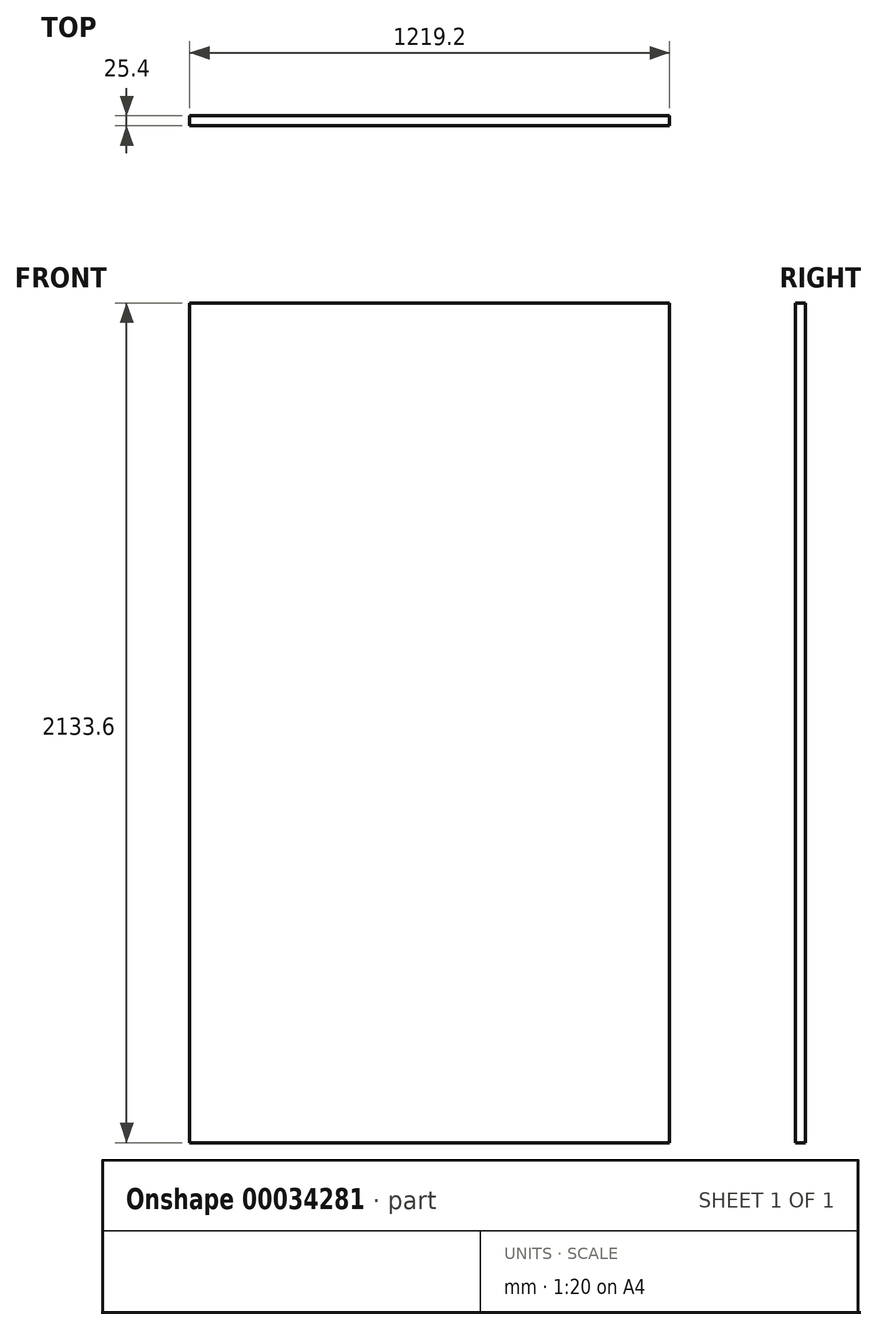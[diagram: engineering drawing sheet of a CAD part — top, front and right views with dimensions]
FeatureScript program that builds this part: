
annotation { "Feature Type Name" : "Feature", "Feature Type Description" : "" }
export const myFeature = defineFeature(function(context is Context, id is Id, definition is map)
    precondition{}
    {
        {
            var Q0;
            Q0=qCreatedBy(makeId("Front.planeOp"),FACE);
            var sketch = newSketch(context, id + "F0", { "sketchPlane" : qUnion([Q0])});
            skLineSegment(sketch, "E0.bottom", {"start": v(0, 0) * mm, "end": v(1219.2, 0) * mm});
            skLineSegment(sketch, "E0.top", {"start": v(0, 2133.6) * mm, "end": v(1219.2, 2133.6) * mm});
            skLineSegment(sketch, "E0.left", {"start": v(0, 0) * mm, "end": v(0, 2133.6) * mm});
            skLineSegment(sketch, "E0.right", {"start": v(1219.2, 0) * mm, "end": v(1219.2, 2133.6) * mm});
            skSolve(sketch);
        }
        {
            var Q0;
            Q0 = qSketchRegion(id + "F0", true);
            extrude(context, id + "F1", {"entities" : qUnion([Q0]), "depth" : 25.4 * mm});
        }
    });
